# Revit family: Haworth_LIM_Light_Y
name_source: partatom
category: Lighting Fixtures
revit_build: Autodesk Revit 2018 (Build: 20170223_1515(x64)
units: mm (PartAtom-declared; Revit-internal decimal feet)

## family parameters
Always vertical = Yes
Cut with Voids When Loaded = No
Light Source = No
OmniClass Number = 23.80.70.11.14
OmniClass Title = General Luminaries, Directional
Part Type = Normal
Room Calculation Point = No
Round Connector Dimension = Use Diameter
Shared = No
Work Plane-Based = No

## types (1)
- LLY1-0013 - Worksurface Mount
    Actual Height = 18 3/4"
    Actual Width = 26 1/2"
    Arm Length = 12 3/8"
    Assembly Code = D5020200
    Description = Haworth LIM Light Y - Worksurface Mount
    Lamp Finish = Haworth _ Metal _ Brushed Aluminum
    Light Source Height = 13 13/16"
    Manufacturer = Haworth
    Model = LLY1-0013
    Post to Centerline = 3"
    Revision Number = 4
    Size = Verify Final Dim. w/ Haworth
    Table Thickness = 1 1/2"
    URL = http://www.haworth.com
    URL - Product = https://www.haworth.com
    Warranty = http://www.haworth.com
    Wattage Comments = 3 or 7.3 Watts; 120 Volt 60 Hertz

## geometry (parser evidence)
native form markers: Sweep x5
no freeform markers — native parametric forms only
